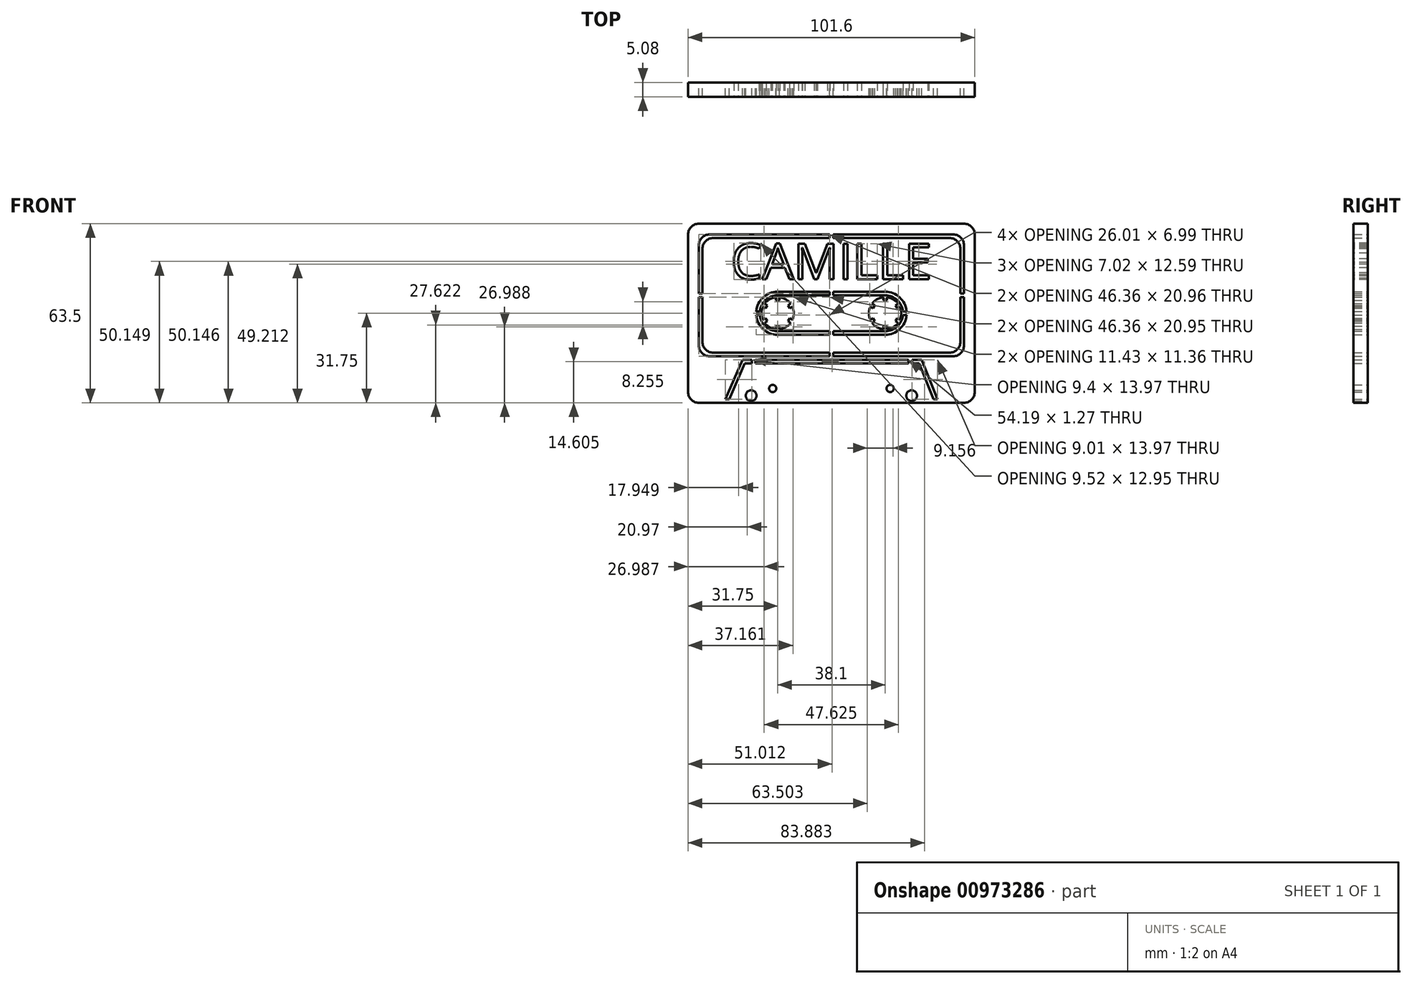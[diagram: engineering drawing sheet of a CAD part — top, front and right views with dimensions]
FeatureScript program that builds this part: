
annotation { "Feature Type Name" : "Feature", "Feature Type Description" : "" }
export const myFeature = defineFeature(function(context is Context, id is Id, definition is map)
    precondition{}
    {
        {
            var Q0;
            Q0=qCreatedBy(makeId("Front.planeOp"),FACE);
            var sketch = newSketch(context, id + "F0", { "sketchPlane" : qUnion([Q0])});
            skLineSegment(sketch, "E0.bottom", {"start": v(47, 31.75) * mm, "end": v(-47, 31.75) * mm});
            skLineSegment(sketch, "E0.top", {"start": v(47, -31.75) * mm, "end": v(-47, -31.75) * mm});
            skLineSegment(sketch, "E0.left", {"start": v(50.8, 27.94) * mm, "end": v(50.8, -27.94) * mm});
            skLineSegment(sketch, "E0.right", {"start": v(-50.8, 27.94) * mm, "end": v(-50.8, -27.94) * mm});
            skPoint(sketch, "E0.middle", {"position": v(0, 0) * mm});
            skPoint(sketch, "E1.visualSharp", {"position": v(50.8, 31.75) * mm});
            skArc(sketch, "E1.filletArc", {"start": v(50.8, 27.94) * mm, "mid": v(49.68, 30.63) * mm, "end": v(47, 31.75) * mm});
            skPoint(sketch, "E2.visualSharp", {"position": v(-50.8, 31.75) * mm});
            skArc(sketch, "E2.filletArc", {"start": v(-47, 31.75) * mm, "mid": v(-49.68, 30.63) * mm, "end": v(-50.8, 27.94) * mm});
            skPoint(sketch, "E3.visualSharp", {"position": v(-50.8, -31.75) * mm});
            skArc(sketch, "E3.filletArc", {"start": v(-50.8, -27.94) * mm, "mid": v(-49.68, -30.63) * mm, "end": v(-47, -31.75) * mm});
            skPoint(sketch, "E4.visualSharp", {"position": v(50.8, -31.75) * mm});
            skArc(sketch, "E4.filletArc", {"start": v(47, -31.75) * mm, "mid": v(49.68, -30.63) * mm, "end": v(50.8, -27.94) * mm});
            skLineSegment(sketch, "E5.bottom", {"start": v(-43.18, 27.94) * mm, "end": v(-0.64, 27.94) * mm});
            skLineSegment(sketch, "E5.top", {"start": v(-43.18, -15.24) * mm, "end": v(-0.64, -15.24) * mm});
            skLineSegment(sketch, "E5.left", {"start": v(-47, 24.13) * mm, "end": v(-47, 6.98) * mm});
            skLineSegment(sketch, "E5.right", {"start": v(47, 24.13) * mm, "end": v(47, 6.99) * mm});
            skLineSegment(sketch, "E6.bottom", {"start": v(-41.91, 26.67) * mm, "end": v(-0.63, 26.67) * mm});
            skLineSegment(sketch, "E6.top", {"start": v(-41.91, -13.97) * mm, "end": v(-0.63, -13.97) * mm});
            skLineSegment(sketch, "E6.left", {"start": v(-45.72, 22.86) * mm, "end": v(-45.72, 6.98) * mm});
            skLineSegment(sketch, "E6.right", {"start": v(45.72, 22.86) * mm, "end": v(45.72, 6.99) * mm});
            skArc(sketch, "E7.filletArc", {"start": v(47, 24.13) * mm, "mid": v(45.87, 26.82) * mm, "end": v(43.18, 27.94) * mm});
            skPoint(sketch, "E8.visualSharp", {"position": v(45.72, 26.67) * mm});
            skArc(sketch, "E8.filletArc", {"start": v(45.72, 22.86) * mm, "mid": v(44.6, 25.55) * mm, "end": v(41.91, 26.67) * mm});
            skPoint(sketch, "E9.visualSharp", {"position": v(47, -15.24) * mm});
            skArc(sketch, "E9.filletArc", {"start": v(43.18, -15.24) * mm, "mid": v(45.87, -14.12) * mm, "end": v(47, -11.43) * mm});
            skPoint(sketch, "E10.visualSharp", {"position": v(45.72, -13.97) * mm});
            skArc(sketch, "E10.filletArc", {"start": v(41.91, -13.97) * mm, "mid": v(44.6, -12.85) * mm, "end": v(45.72, -10.16) * mm});
            skPoint(sketch, "E11.visualSharp", {"position": v(-47, -15.24) * mm});
            skArc(sketch, "E11.filletArc", {"start": v(-47, -11.43) * mm, "mid": v(-45.87, -14.12) * mm, "end": v(-43.18, -15.24) * mm});
            skPoint(sketch, "E12.visualSharp", {"position": v(-45.72, -13.97) * mm});
            skArc(sketch, "E12.filletArc", {"start": v(-45.72, -10.16) * mm, "mid": v(-44.6, -12.85) * mm, "end": v(-41.91, -13.97) * mm});
            skArc(sketch, "E13.filletArc", {"start": v(-43.18, 27.94) * mm, "mid": v(-45.87, 26.82) * mm, "end": v(-47, 24.13) * mm});
            skPoint(sketch, "E14.visualSharp", {"position": v(-45.72, 26.67) * mm});
            skArc(sketch, "E14.filletArc", {"start": v(-41.91, 26.67) * mm, "mid": v(-44.6, 25.55) * mm, "end": v(-45.72, 22.86) * mm});
            skLineSegment(sketch, "E15", {"start": v(0.64, -15.24) * mm, "end": v(0.64, -13.97) * mm});
            skLineSegment(sketch, "E16", {"start": v(-0.64, -15.24) * mm, "end": v(-0.64, -13.97) * mm});
            skLineSegment(sketch, "E17.trimOffspring", {"start": v(-0.64, 26.67) * mm, "end": v(-0.64, 27.94) * mm});
            skLineSegment(sketch, "E18.trimOffspring", {"start": v(0.64, 26.67) * mm, "end": v(0.64, 27.94) * mm});
            skLineSegment(sketch, "E19.trimOffspring", {"start": v(0.63, -13.97) * mm, "end": v(41.91, -13.97) * mm});
            skLineSegment(sketch, "E20.trimOffspring", {"start": v(0.64, -15.24) * mm, "end": v(43.18, -15.24) * mm});
            skLineSegment(sketch, "E21.trimOffspring", {"start": v(0.64, 27.94) * mm, "end": v(43.18, 27.94) * mm});
            skLineSegment(sketch, "E22.trimOffspring", {"start": v(0.63, 26.67) * mm, "end": v(41.91, 26.67) * mm});
            skLineSegment(sketch, "E23", {"start": v(-47, 6.98) * mm, "end": v(-45.72, 6.99) * mm});
            skLineSegment(sketch, "E24", {"start": v(-47, 5.71) * mm, "end": v(-45.72, 5.71) * mm});
            skLineSegment(sketch, "E25.trimOffspring", {"start": v(45.72, 6.99) * mm, "end": v(47, 6.99) * mm});
            skLineSegment(sketch, "E26.trimOffspring", {"start": v(45.72, 5.72) * mm, "end": v(47, 5.72) * mm});
            skPoint(sketch, "E27.orphan", {"position": v(48.52, 5.72) * mm});
            skPoint(sketch, "E28.orphan", {"position": v(48.52, 6.99) * mm});
            skLineSegment(sketch, "E29.trimOffspring", {"start": v(47, 5.72) * mm, "end": v(47, -11.43) * mm});
            skLineSegment(sketch, "E30.trimOffspring", {"start": v(45.72, 5.72) * mm, "end": v(45.72, -10.16) * mm});
            skLineSegment(sketch, "E31.trimOffspring", {"start": v(-45.72, 5.71) * mm, "end": v(-45.72, -10.16) * mm});
            skLineSegment(sketch, "E32.trimOffspring", {"start": v(-47, 5.71) * mm, "end": v(-47, -11.43) * mm});
            skLineSegment(sketch, "E33.bottom", {"start": v(-19.05, 6.35) * mm, "end": v(-0.63, 6.35) * mm});
            skLineSegment(sketch, "E33.top", {"start": v(-19.05, -6.35) * mm, "end": v(-0.63, -6.35) * mm});
            skLineSegment(sketch, "E34.bottom", {"start": v(-19.05, 7.62) * mm, "end": v(-0.63, 7.62) * mm});
            skLineSegment(sketch, "E34.top", {"start": v(-19.05, -7.62) * mm, "end": v(-0.63, -7.62) * mm});
            skLineSegment(sketch, "E35", {"start": v(-0.63, 7.62) * mm, "end": v(-0.63, 6.35) * mm});
            skLineSegment(sketch, "E36", {"start": v(0.63, 7.62) * mm, "end": v(0.63, 6.35) * mm});
            skLineSegment(sketch, "E37.trimOffspring", {"start": v(-0.63, -6.35) * mm, "end": v(-0.63, -7.62) * mm});
            skLineSegment(sketch, "E38.trimOffspring", {"start": v(0.63, -6.35) * mm, "end": v(0.63, -7.62) * mm});
            skLineSegment(sketch, "E39.trimOffspring", {"start": v(0.64, -7.62) * mm, "end": v(19.05, -7.62) * mm});
            skLineSegment(sketch, "E40.trimOffspring", {"start": v(0.63, -6.35) * mm, "end": v(19.05, -6.35) * mm});
            skLineSegment(sketch, "E41.trimOffspring", {"start": v(0.63, 7.62) * mm, "end": v(19.05, 7.62) * mm});
            skLineSegment(sketch, "E42.trimOffspring", {"start": v(0.64, 6.35) * mm, "end": v(23.26, 6.35) * mm});
            skArc(sketch, "E43", {"start": v(-19.69, 5.68) * mm, "mid": v(-21.9, 4.95) * mm, "end": v(-23.65, 3.39) * mm});
            skArc(sketch, "E44", {"start": v(18.41, 5.68) * mm, "mid": v(16.2, 4.95) * mm, "end": v(14.45, 3.39) * mm});
            skArc(sketch, "E45", {"start": v(-19.05, 7.62) * mm, "mid": v(-24.2, 5.6) * mm, "end": v(-26.64, 0.64) * mm});
            skArc(sketch, "E46", {"start": v(-19.05, 6.35) * mm, "mid": v(-23.3, 4.7) * mm, "end": v(-25.37, 0.63) * mm});
            skArc(sketch, "E47", {"start": v(19.05, 7.62) * mm, "mid": v(24.2, 5.6) * mm, "end": v(26.64, 0.64) * mm});
            skArc(sketch, "E48", {"start": v(19.05, 6.35) * mm, "mid": v(23.3, 4.7) * mm, "end": v(25.37, 0.63) * mm});
            skLineSegment(sketch, "E49", {"start": v(-26.64, 0.64) * mm, "end": v(-25.37, 0.64) * mm});
            skLineSegment(sketch, "E50", {"start": v(-26.64, -0.64) * mm, "end": v(-25.37, -0.64) * mm});
            skArc(sketch, "E51.trimOffspring", {"start": v(-26.64, -0.64) * mm, "mid": v(-24.2, -5.6) * mm, "end": v(-19.05, -7.62) * mm});
            skArc(sketch, "E52.trimOffspring", {"start": v(-25.37, -0.64) * mm, "mid": v(-23.3, -4.7) * mm, "end": v(-19.05, -6.35) * mm});
            skLineSegment(sketch, "E53.trimOffspring", {"start": v(25.37, 0.64) * mm, "end": v(26.64, 0.64) * mm});
            skLineSegment(sketch, "E54.trimOffspring", {"start": v(25.37, -0.64) * mm, "end": v(26.64, -0.64) * mm});
            skArc(sketch, "E55.trimOffspring", {"start": v(25.37, -0.64) * mm, "mid": v(23.3, -4.7) * mm, "end": v(19.05, -6.35) * mm});
            skArc(sketch, "E56.trimOffspring", {"start": v(26.64, -0.64) * mm, "mid": v(24.2, -5.6) * mm, "end": v(19.05, -7.62) * mm});
            skLineSegment(sketch, "E57", {"start": v(-18.41, 5.68) * mm, "end": v(-18.41, 4.57) * mm});
            skLineSegment(sketch, "E58", {"start": v(-18.41, 4.57) * mm, "end": v(-19.69, 4.57) * mm});
            skLineSegment(sketch, "E59", {"start": v(-19.69, 4.57) * mm, "end": v(-19.69, 5.68) * mm});
            skLineSegment(sketch, "E60.MirrorCS", {"start": v(18.41, 5.68) * mm, "end": v(18.41, 4.57) * mm});
            skLineSegment(sketch, "E61.MirrorCS", {"start": v(18.41, 4.57) * mm, "end": v(19.69, 4.57) * mm});
            skLineSegment(sketch, "E62.MirrorCS", {"start": v(19.69, 4.57) * mm, "end": v(19.69, 5.68) * mm});
            skLineSegment(sketch, "E63.1.0", {"start": v(-23.65, 3.39) * mm, "end": v(-22.7, 2.84) * mm});
            skLineSegment(sketch, "E63.1.1", {"start": v(-22.7, 2.84) * mm, "end": v(-23.33, 1.74) * mm});
            skLineSegment(sketch, "E63.1.2", {"start": v(-23.33, 1.74) * mm, "end": v(-24.29, 2.29) * mm});
            skLineSegment(sketch, "E63.2.0", {"start": v(-24.29, -2.29) * mm, "end": v(-23.33, -1.74) * mm});
            skLineSegment(sketch, "E63.2.1", {"start": v(-23.33, -1.74) * mm, "end": v(-22.7, -2.84) * mm});
            skLineSegment(sketch, "E63.2.2", {"start": v(-22.7, -2.84) * mm, "end": v(-23.65, -3.39) * mm});
            skLineSegment(sketch, "E63.3.0", {"start": v(-19.69, -5.68) * mm, "end": v(-19.69, -4.57) * mm});
            skLineSegment(sketch, "E63.3.1", {"start": v(-19.69, -4.57) * mm, "end": v(-18.41, -4.57) * mm});
            skLineSegment(sketch, "E63.3.2", {"start": v(-18.41, -4.57) * mm, "end": v(-18.41, -5.68) * mm});
            skLineSegment(sketch, "E63.4.0", {"start": v(-14.45, -3.39) * mm, "end": v(-15.4, -2.84) * mm});
            skLineSegment(sketch, "E63.4.1", {"start": v(-15.4, -2.84) * mm, "end": v(-14.77, -1.74) * mm});
            skLineSegment(sketch, "E63.4.2", {"start": v(-14.77, -1.74) * mm, "end": v(-13.81, -2.29) * mm});
            skLineSegment(sketch, "E63.5.0", {"start": v(-13.81, 2.29) * mm, "end": v(-14.77, 1.74) * mm});
            skLineSegment(sketch, "E63.5.1", {"start": v(-14.77, 1.74) * mm, "end": v(-15.4, 2.84) * mm});
            skLineSegment(sketch, "E63.5.2", {"start": v(-15.4, 2.84) * mm, "end": v(-14.45, 3.39) * mm});
            skArc(sketch, "E64.trimOffspring", {"start": v(-14.45, 3.39) * mm, "mid": v(-16.2, 4.95) * mm, "end": v(-18.41, 5.68) * mm});
            skArc(sketch, "E65.trimOffspring", {"start": v(-13.81, -2.29) * mm, "mid": v(-13.33, 0) * mm, "end": v(-13.81, 2.29) * mm});
            skArc(sketch, "E66.trimOffspring", {"start": v(-18.41, -5.68) * mm, "mid": v(-16.2, -4.95) * mm, "end": v(-14.45, -3.39) * mm});
            skArc(sketch, "E67.trimOffspring", {"start": v(-23.65, -3.39) * mm, "mid": v(-21.9, -4.95) * mm, "end": v(-19.69, -5.68) * mm});
            skArc(sketch, "E68.trimOffspring", {"start": v(-24.29, 2.29) * mm, "mid": v(-24.77, 0) * mm, "end": v(-24.29, -2.29) * mm});
            skLineSegment(sketch, "E69.1.0", {"start": v(15.4, 2.84) * mm, "end": v(14.45, 3.39) * mm});
            skLineSegment(sketch, "E69.1.1", {"start": v(14.77, 1.74) * mm, "end": v(15.4, 2.84) * mm});
            skLineSegment(sketch, "E69.1.2", {"start": v(13.81, 2.29) * mm, "end": v(14.77, 1.74) * mm});
            skLineSegment(sketch, "E69.2.0", {"start": v(14.77, -1.74) * mm, "end": v(13.81, -2.29) * mm});
            skLineSegment(sketch, "E69.2.1", {"start": v(15.4, -2.84) * mm, "end": v(14.77, -1.74) * mm});
            skLineSegment(sketch, "E69.2.2", {"start": v(14.45, -3.39) * mm, "end": v(15.4, -2.84) * mm});
            skLineSegment(sketch, "E69.3.0", {"start": v(18.41, -4.57) * mm, "end": v(18.41, -5.68) * mm});
            skLineSegment(sketch, "E69.3.1", {"start": v(19.69, -4.57) * mm, "end": v(18.41, -4.57) * mm});
            skLineSegment(sketch, "E69.3.2", {"start": v(19.69, -5.68) * mm, "end": v(19.69, -4.57) * mm});
            skLineSegment(sketch, "E69.4.0", {"start": v(22.7, -2.84) * mm, "end": v(23.65, -3.39) * mm});
            skLineSegment(sketch, "E69.4.1", {"start": v(23.33, -1.74) * mm, "end": v(22.7, -2.84) * mm});
            skLineSegment(sketch, "E69.4.2", {"start": v(24.29, -2.29) * mm, "end": v(23.33, -1.74) * mm});
            skLineSegment(sketch, "E69.5.0", {"start": v(23.33, 1.74) * mm, "end": v(24.29, 2.29) * mm});
            skLineSegment(sketch, "E69.5.1", {"start": v(22.7, 2.84) * mm, "end": v(23.33, 1.74) * mm});
            skLineSegment(sketch, "E69.5.2", {"start": v(23.65, 3.39) * mm, "end": v(22.7, 2.84) * mm});
            skArc(sketch, "E70.trimOffspring", {"start": v(23.65, 3.39) * mm, "mid": v(21.9, 4.95) * mm, "end": v(19.69, 5.68) * mm});
            skArc(sketch, "E71.trimOffspring", {"start": v(24.29, -2.29) * mm, "mid": v(24.77, 0) * mm, "end": v(24.29, 2.29) * mm});
            skArc(sketch, "E72.trimOffspring", {"start": v(19.69, -5.68) * mm, "mid": v(21.9, -4.95) * mm, "end": v(23.65, -3.39) * mm});
            skArc(sketch, "E73.trimOffspring", {"start": v(14.45, -3.39) * mm, "mid": v(16.2, -4.95) * mm, "end": v(18.41, -5.68) * mm});
            skArc(sketch, "E74.trimOffspring", {"start": v(13.81, 2.29) * mm, "mid": v(13.33, 0) * mm, "end": v(13.81, -2.29) * mm});
            skLineSegment(sketch, "E75", {"start": v(-37.55, -30.48) * mm, "end": v(-31.53, -16.51) * mm});
            skLineSegment(sketch, "E76", {"start": v(-31.53, -16.51) * mm, "end": v(-28.15, -16.51) * mm});
            skLineSegment(sketch, "E77", {"start": v(31.97, -16.5) * mm, "end": v(37.59, -30.48) * mm});
            skLineSegment(sketch, "E78", {"start": v(-36.17, -30.48) * mm, "end": v(-30.7, -17.78) * mm});
            skLineSegment(sketch, "E79", {"start": v(-30.7, -17.78) * mm, "end": v(-28.15, -17.78) * mm});
            skLineSegment(sketch, "E80", {"start": v(31.12, -17.78) * mm, "end": v(36.22, -30.48) * mm});
            skLineSegment(sketch, "E81", {"start": v(-37.55, -30.48) * mm, "end": v(-36.17, -30.48) * mm});
            skLineSegment(sketch, "E82.trimOffspring", {"start": v(36.22, -30.48) * mm, "end": v(37.59, -30.48) * mm});
            skPoint(sketch, "E83.orphan", {"position": v(-38.1, -31.75) * mm});
            skPoint(sketch, "E84.orphan", {"position": v(38.1, -31.75) * mm});
            skLineSegment(sketch, "E85", {"start": v(-28.15, -17.78) * mm, "end": v(-28.15, -16.51) * mm});
            skLineSegment(sketch, "E86", {"start": v(-26.88, -16.51) * mm, "end": v(-26.88, -17.78) * mm});
            skLineSegment(sketch, "E87.trimOffspring", {"start": v(-26.88, -16.51) * mm, "end": v(27.3, -16.5) * mm});
            skLineSegment(sketch, "E88.trimOffspring", {"start": v(-26.88, -17.78) * mm, "end": v(27.3, -17.78) * mm});
            skLineSegment(sketch, "E89.MirrorCS", {"start": v(27.3, -16.5) * mm, "end": v(27.3, -17.78) * mm});
            skLineSegment(sketch, "E90.MirrorCS", {"start": v(28.58, -17.78) * mm, "end": v(28.58, -16.5) * mm});
            skLineSegment(sketch, "E91.trimOffspring", {"start": v(28.58, -16.5) * mm, "end": v(31.97, -16.5) * mm});
            skLineSegment(sketch, "E92.trimOffspring", {"start": v(28.58, -17.78) * mm, "end": v(31.12, -17.78) * mm});
            skCircle(sketch, "E93", {"center": v(-28.44, -29.21) * mm, "radius": 1.9 * mm});
            skCircle(sketch, "E94", {"center": v(-20.82, -26.67) * mm, "radius": 1.27 * mm});
            skCircle(sketch, "E95.MirrorC", {"center": v(20.82, -26.67) * mm, "radius": 1.27 * mm});
            skCircle(sketch, "E96.MirrorC", {"center": v(28.44, -29.21) * mm, "radius": 1.9 * mm});
            skSolve(sketch);
        }
        {
            var Q0;
            Q0=qSketchRegion(id+"F0",true);
            extrude(context, id + "F1", {"entities" : qUnion([Q0]), "depth" : 5.08 * mm, "offsetDistance" : 25.4 * mm});
        }
        {
            var Q0;
            Q0=makeQuery(id+"F1.opExtrude","CAP_FACE",FACE,{"disambiguationData":[OSD([sQuery(id+"F0.wireOp",EDGE,"E0.bottom"),sQuery(id+"F0.wireOp",EDGE,"E0.top"),sQuery(id+"F0.wireOp",EDGE,"E0.left"),sQuery(id+"F0.wireOp",EDGE,"E0.right"),sQuery(id+"F0.wireOp",EDGE,"E1.filletArc"),sQuery(id+"F0.wireOp",EDGE,"E2.filletArc"),sQuery(id+"F0.wireOp",EDGE,"E3.filletArc"),sQuery(id+"F0.wireOp",EDGE,"E4.filletArc"),sQuery(id+"F0.wireOp",EDGE,"E5.bottom"),sQuery(id+"F0.wireOp",EDGE,"E5.top"),sQuery(id+"F0.wireOp",EDGE,"E5.left"),sQuery(id+"F0.wireOp",EDGE,"E5.right"),sQuery(id+"F0.wireOp",EDGE,"E6.bottom"),sQuery(id+"F0.wireOp",EDGE,"E6.top"),sQuery(id+"F0.wireOp",EDGE,"E6.left"),sQuery(id+"F0.wireOp",EDGE,"E6.right"),sQuery(id+"F0.wireOp",EDGE,"E7.filletArc"),sQuery(id+"F0.wireOp",EDGE,"E8.filletArc"),sQuery(id+"F0.wireOp",EDGE,"E9.filletArc"),sQuery(id+"F0.wireOp",EDGE,"E10.filletArc"),sQuery(id+"F0.wireOp",EDGE,"E11.filletArc"),sQuery(id+"F0.wireOp",EDGE,"E12.filletArc"),sQuery(id+"F0.wireOp",EDGE,"E13.filletArc"),sQuery(id+"F0.wireOp",EDGE,"E14.filletArc"),sQuery(id+"F0.wireOp",EDGE,"E15"),sQuery(id+"F0.wireOp",EDGE,"E16"),sQuery(id+"F0.wireOp",EDGE,"E17.trimOffspring"),sQuery(id+"F0.wireOp",EDGE,"E18.trimOffspring"),sQuery(id+"F0.wireOp",EDGE,"E19.trimOffspring"),sQuery(id+"F0.wireOp",EDGE,"E20.trimOffspring"),sQuery(id+"F0.wireOp",EDGE,"E21.trimOffspring"),sQuery(id+"F0.wireOp",EDGE,"E22.trimOffspring"),sQuery(id+"F0.wireOp",EDGE,"E23"),sQuery(id+"F0.wireOp",EDGE,"E24"),sQuery(id+"F0.wireOp",EDGE,"E25.trimOffspring"),sQuery(id+"F0.wireOp",EDGE,"E26.trimOffspring"),sQuery(id+"F0.wireOp",EDGE,"E29.trimOffspring"),sQuery(id+"F0.wireOp",EDGE,"E30.trimOffspring"),sQuery(id+"F0.wireOp",EDGE,"E31.trimOffspring"),sQuery(id+"F0.wireOp",EDGE,"E32.trimOffspring"),sQuery(id+"F0.wireOp",EDGE,"E33.bottom"),sQuery(id+"F0.wireOp",EDGE,"E33.top"),sQuery(id+"F0.wireOp",EDGE,"E34.bottom"),sQuery(id+"F0.wireOp",EDGE,"E34.top"),sQuery(id+"F0.wireOp",EDGE,"E35"),sQuery(id+"F0.wireOp",EDGE,"E36"),sQuery(id+"F0.wireOp",EDGE,"E37.trimOffspring"),sQuery(id+"F0.wireOp",EDGE,"E38.trimOffspring"),sQuery(id+"F0.wireOp",EDGE,"E39.trimOffspring"),sQuery(id+"F0.wireOp",EDGE,"E40.trimOffspring"),sQuery(id+"F0.wireOp",EDGE,"E41.trimOffspring"),sQuery(id+"F0.wireOp",EDGE,"E42.trimOffspring"),sQuery(id+"F0.wireOp",EDGE,"E43"),sQuery(id+"F0.wireOp",EDGE,"E44"),sQuery(id+"F0.wireOp",EDGE,"E45"),sQuery(id+"F0.wireOp",EDGE,"E46"),sQuery(id+"F0.wireOp",EDGE,"E47"),sQuery(id+"F0.wireOp",EDGE,"E48"),sQuery(id+"F0.wireOp",EDGE,"E49"),sQuery(id+"F0.wireOp",EDGE,"E50"),sQuery(id+"F0.wireOp",EDGE,"E51.trimOffspring"),sQuery(id+"F0.wireOp",EDGE,"E52.trimOffspring"),sQuery(id+"F0.wireOp",EDGE,"E53.trimOffspring"),sQuery(id+"F0.wireOp",EDGE,"E54.trimOffspring"),sQuery(id+"F0.wireOp",EDGE,"E55.trimOffspring"),sQuery(id+"F0.wireOp",EDGE,"E56.trimOffspring"),sQuery(id+"F0.wireOp",EDGE,"E57"),sQuery(id+"F0.wireOp",EDGE,"E58"),sQuery(id+"F0.wireOp",EDGE,"E59"),sQuery(id+"F0.wireOp",EDGE,"E60.MirrorCS"),sQuery(id+"F0.wireOp",EDGE,"E61.MirrorCS"),sQuery(id+"F0.wireOp",EDGE,"E62.MirrorCS"),sQuery(id+"F0.wireOp",EDGE,"E63.1.0"),sQuery(id+"F0.wireOp",EDGE,"E63.1.1"),sQuery(id+"F0.wireOp",EDGE,"E63.1.2"),sQuery(id+"F0.wireOp",EDGE,"E63.2.0"),sQuery(id+"F0.wireOp",EDGE,"E63.2.1"),sQuery(id+"F0.wireOp",EDGE,"E63.2.2"),sQuery(id+"F0.wireOp",EDGE,"E63.3.0"),sQuery(id+"F0.wireOp",EDGE,"E63.3.1"),sQuery(id+"F0.wireOp",EDGE,"E63.3.2"),sQuery(id+"F0.wireOp",EDGE,"E63.4.0"),sQuery(id+"F0.wireOp",EDGE,"E63.4.1"),sQuery(id+"F0.wireOp",EDGE,"E63.4.2"),sQuery(id+"F0.wireOp",EDGE,"E63.5.0"),sQuery(id+"F0.wireOp",EDGE,"E63.5.1"),sQuery(id+"F0.wireOp",EDGE,"E63.5.2"),sQuery(id+"F0.wireOp",EDGE,"E64.trimOffspring"),sQuery(id+"F0.wireOp",EDGE,"E65.trimOffspring"),sQuery(id+"F0.wireOp",EDGE,"E66.trimOffspring"),sQuery(id+"F0.wireOp",EDGE,"E67.trimOffspring"),sQuery(id+"F0.wireOp",EDGE,"E68.trimOffspring"),sQuery(id+"F0.wireOp",EDGE,"E69.1.0"),sQuery(id+"F0.wireOp",EDGE,"E69.1.1"),sQuery(id+"F0.wireOp",EDGE,"E69.1.2"),sQuery(id+"F0.wireOp",EDGE,"E69.2.0"),sQuery(id+"F0.wireOp",EDGE,"E69.2.1"),sQuery(id+"F0.wireOp",EDGE,"E69.2.2"),sQuery(id+"F0.wireOp",EDGE,"E69.3.0"),sQuery(id+"F0.wireOp",EDGE,"E69.3.1"),sQuery(id+"F0.wireOp",EDGE,"E69.3.2"),sQuery(id+"F0.wireOp",EDGE,"E69.4.0"),sQuery(id+"F0.wireOp",EDGE,"E69.4.1"),sQuery(id+"F0.wireOp",EDGE,"E69.4.2"),sQuery(id+"F0.wireOp",EDGE,"E69.5.0"),sQuery(id+"F0.wireOp",EDGE,"E69.5.1"),sQuery(id+"F0.wireOp",EDGE,"E69.5.2"),sQuery(id+"F0.wireOp",EDGE,"E70.trimOffspring"),sQuery(id+"F0.wireOp",EDGE,"E71.trimOffspring"),sQuery(id+"F0.wireOp",EDGE,"E72.trimOffspring"),sQuery(id+"F0.wireOp",EDGE,"E73.trimOffspring"),sQuery(id+"F0.wireOp",EDGE,"E74.trimOffspring"),sQuery(id+"F0.wireOp",EDGE,"E75"),sQuery(id+"F0.wireOp",EDGE,"E76"),sQuery(id+"F0.wireOp",EDGE,"E77"),sQuery(id+"F0.wireOp",EDGE,"E78"),sQuery(id+"F0.wireOp",EDGE,"E79"),sQuery(id+"F0.wireOp",EDGE,"E80"),sQuery(id+"F0.wireOp",EDGE,"E81"),sQuery(id+"F0.wireOp",EDGE,"E82.trimOffspring"),sQuery(id+"F0.wireOp",EDGE,"E85"),sQuery(id+"F0.wireOp",EDGE,"E86"),sQuery(id+"F0.wireOp",EDGE,"E87.trimOffspring"),sQuery(id+"F0.wireOp",EDGE,"E88.trimOffspring"),sQuery(id+"F0.wireOp",EDGE,"E89.MirrorCS"),sQuery(id+"F0.wireOp",EDGE,"E90.MirrorCS"),sQuery(id+"F0.wireOp",EDGE,"E91.trimOffspring"),sQuery(id+"F0.wireOp",EDGE,"E92.trimOffspring"),sQuery(id+"F0.wireOp",EDGE,"E93"),sQuery(id+"F0.wireOp",EDGE,"E94"),sQuery(id+"F0.wireOp",EDGE,"E95.MirrorC"),sQuery(id+"F0.wireOp",EDGE,"E96.MirrorC")])],"isStart":false});
            var sketch = newSketch(context, id + "F2", { "sketchPlane" : qUnion([Q0])});
            skText(sketch, "E97", { "text": "CAMILLE", "fontName": "OpenSans-Regular.ttf"});
            const initialGuessF2  = {"E97": [-0.03567, 0.0121, 1, 0, 0.0127]};
            skSetInitialGuess(sketch, initialGuessF2);
            skSolve(sketch);
        }
        {
            var Q0;
            Q0=qSketchRegion(id+"F2",true);
            extrude(context, id + "F3", {"entities" : qUnion([Q0]), "operationType" : NewBodyOperationType.REMOVE, "oppositeDirection" : true, "depth" : 25.4 * mm, "offsetDistance" : 25.4 * mm});
        }
    });
